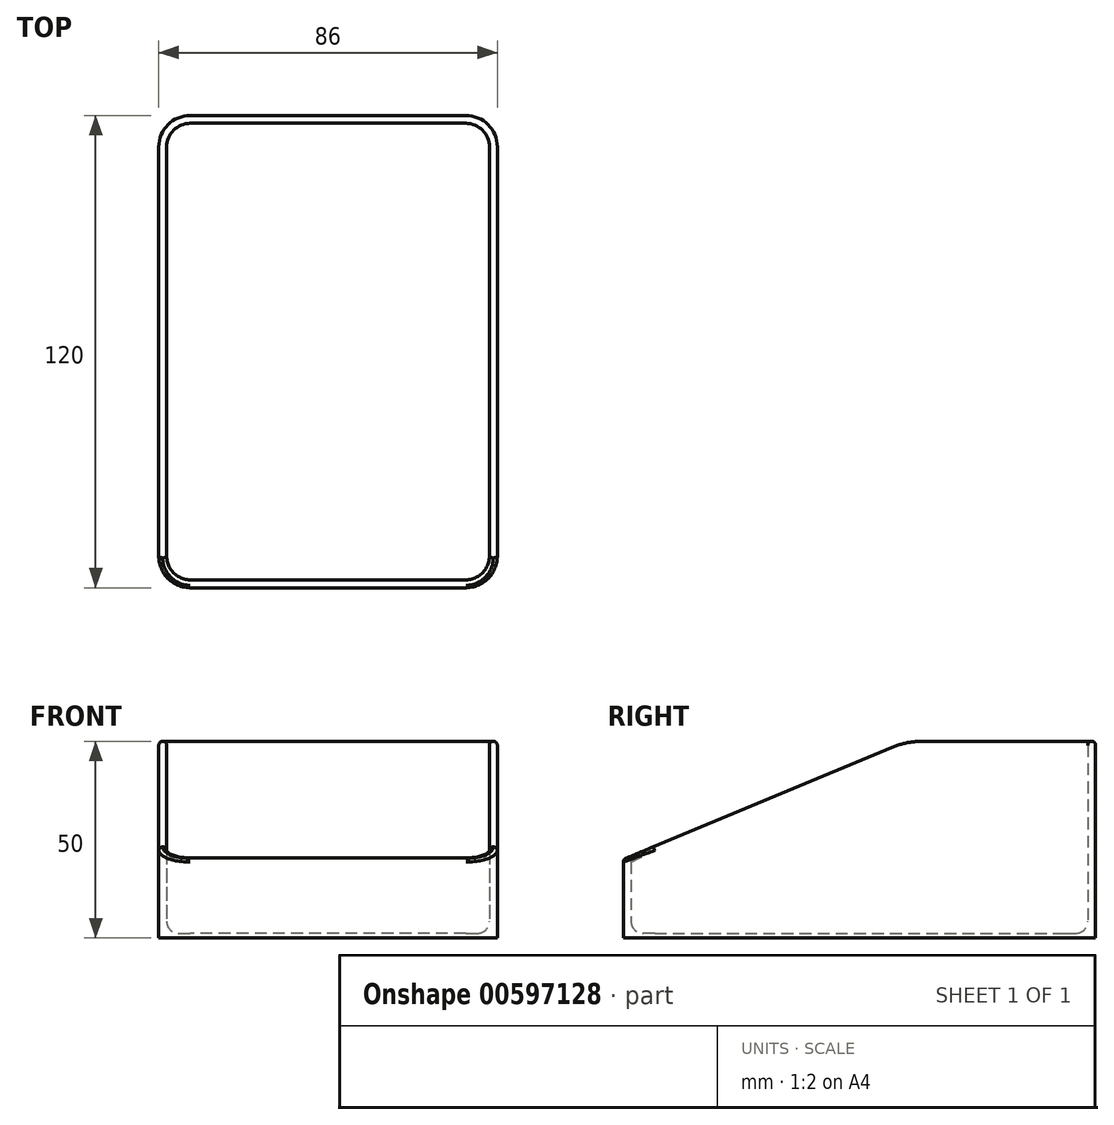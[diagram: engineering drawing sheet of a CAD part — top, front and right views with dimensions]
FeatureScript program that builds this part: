
annotation { "Feature Type Name" : "Feature", "Feature Type Description" : "" }
export const myFeature = defineFeature(function(context is Context, id is Id, definition is map)
    precondition{}
    {
        {
            var Q0;
            Q0=qCreatedBy(makeId("Right.planeOp"),FACE);
            var sketch = newSketch(context, id + "F0", { "sketchPlane" : qUnion([Q0])});
            skLineSegment(sketch, "E0", {"start": v(-60, 0) * mm, "end": v(60, 0) * mm});
            skLineSegment(sketch, "E1", {"start": v(60, 0) * mm, "end": v(60, 50) * mm});
            skLineSegment(sketch, "E2", {"start": v(60, 50) * mm, "end": v(16, 50) * mm});
            skLineSegment(sketch, "E3", {"start": v(8.3, 48.46) * mm, "end": v(-60, 20) * mm});
            skLineSegment(sketch, "E4", {"start": v(-60, 20) * mm, "end": v(-60, 0) * mm});
            skPoint(sketch, "E5.visualSharp", {"position": v(12, 50) * mm});
            skArc(sketch, "E5.filletArc", {"start": v(16, 50) * mm, "mid": v(12.08, 49.61) * mm, "end": v(8.3, 48.46) * mm});
            skSolve(sketch);
        }
        {
            var Q0;
            Q0 = qSketchRegion(id + "F0", true);
            extrude(context, id + "F1", {"entities" : qUnion([Q0]), "depth" : 86 * mm, "offsetDistance" : 25 * mm, "symmetric" : true});
        }
        {
            var Q0;
            Q0=makeQuery(id+"F1.opExtrude","CAP_EDGE",EDGE,{"disambiguationData":[OSD([sQuery(id+"F0.wireOp",EDGE,"E4")])],"isStart":true});
            var Q1;
            Q1=makeQuery(id+"F1.opExtrude","CAP_EDGE",EDGE,{"disambiguationData":[OSD([sQuery(id+"F0.wireOp",EDGE,"E4")])],"isStart":false});
            var Q2;
            Q2=makeQuery(id+"F1.opExtrude","CAP_EDGE",EDGE,{"disambiguationData":[OSD([sQuery(id+"F0.wireOp",EDGE,"E1")])],"isStart":false});
            var Q3;
            Q3=makeQuery(id+"F1.opExtrude","CAP_EDGE",EDGE,{"disambiguationData":[OSD([sQuery(id+"F0.wireOp",EDGE,"E1")])],"isStart":true});
            fillet(context, id + "F2", {"entities" : qUnion([Q0, Q1, Q2, Q3]), "radius" : 8 * mm, "tangentPropagation" : true, "allowEdgeOverflow" : false});
        }
        {
            var Q0;
            Q0=qCreatedBy(makeId("Top.planeOp"),FACE);
            var sketch = newSketch(context, id + "F3", { "sketchPlane" : qUnion([Q0])});
            skArc(sketch, "E6.0", {"start": v(41, -52) * mm, "mid": v(39.24, -56.24) * mm, "end": v(35, -58) * mm});
            skLineSegment(sketch, "E6.1", {"start": v(41, -52) * mm, "end": v(41, 52) * mm});
            skLineSegment(sketch, "E6.2", {"start": v(35, -58) * mm, "end": v(-35, -58) * mm});
            skArc(sketch, "E6.3", {"start": v(35, 58) * mm, "mid": v(39.24, 56.24) * mm, "end": v(41, 52) * mm});
            skArc(sketch, "E6.4", {"start": v(-35, -58) * mm, "mid": v(-39.24, -56.24) * mm, "end": v(-41, -52) * mm});
            skLineSegment(sketch, "E6.5", {"start": v(-41, -52) * mm, "end": v(-41, 52) * mm});
            skArc(sketch, "E6.6", {"start": v(-41, 52) * mm, "mid": v(-39.24, 56.24) * mm, "end": v(-35, 58) * mm});
            skLineSegment(sketch, "E6.7", {"start": v(35, 58) * mm, "end": v(-35, 58) * mm});
            skSolve(sketch);
        }
        {
            var Q0;
            Q0 = qSketchRegion(id + "F3", true);
            extrude(context, id + "F4", {"entities" : qUnion([Q0]), "operationType" : NewBodyOperationType.REMOVE, "endBound" : BoundingType.THROUGH_ALL, "depth" : 25 * mm, "offsetDistance" : 25 * mm, "hasSecondDirection" : true, "secondDirectionOppositeDirection" : false, "secondDirectionDepth" : 1.2 * mm});
        }
        {
            var Q0;
            Q0=makeQuery(id+"F4.boolean.opBoolean","COPY",EDGE,{"derivedFrom":makeQuery(id+"F4.opExtrude","CAP_EDGE",EDGE,{"disambiguationData":[OSD([sQuery(id+"F3.wireOp",EDGE,"E6.5")])],"isStart":true})});
            fillet(context, id + "F5", {"entities" : qUnion([Q0]), "radius" : 3 * mm, "tangentPropagation" : true, "allowEdgeOverflow" : false});
        }
        {
            var Q0;
            Q0=makeQuery(id+"F1.opExtrude","CAP_EDGE",EDGE,{"disambiguationData":[OSD([sQuery(id+"F0.wireOp",EDGE,"E2")])],"isStart":true});
            var Q1;
            Q1=makeQuery(id+"F4.boolean.opBoolean","INTERSECT",EDGE,{"derivedFrom":[makeQuery(id+"F1.opExtrude","SWEPT_FACE",FACE,{"disambiguationData":[OSD([sQuery(id+"F0.wireOp",EDGE,"E3")])]}),makeQuery(id+"F4.opExtrude","SWEPT_FACE",FACE,{"disambiguationData":[OSD([sQuery(id+"F3.wireOp",EDGE,"E6.5")])]})]});
            fillet(context, id + "F6", {"entities" : qUnion([Q0, Q1]), "radius" : 1 * mm, "tangentPropagation" : true, "allowEdgeOverflow" : false});
        }
    });
